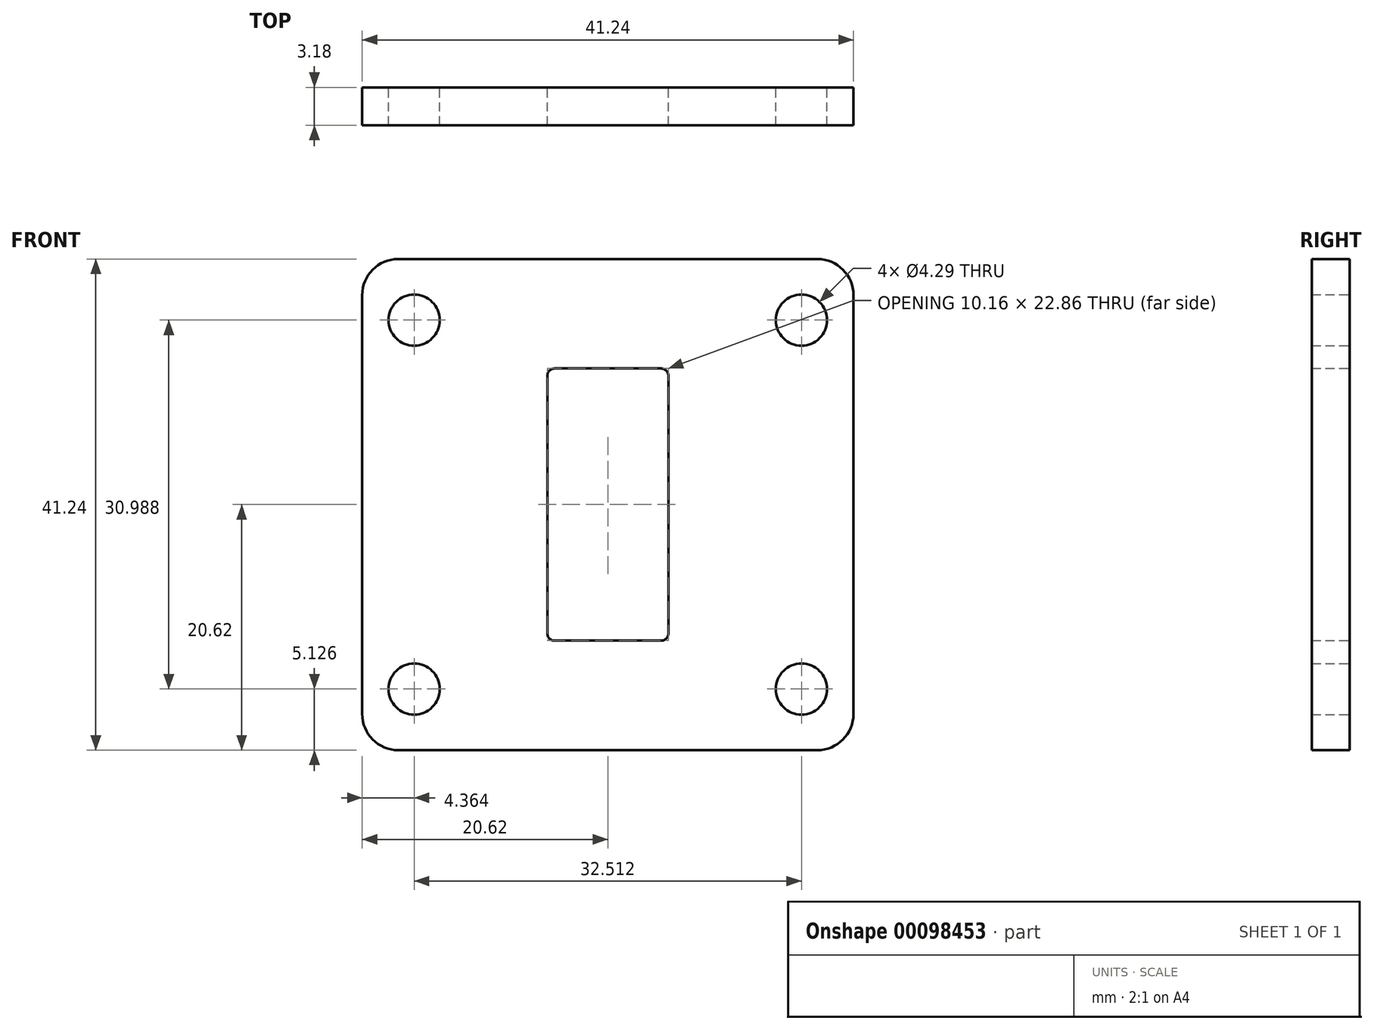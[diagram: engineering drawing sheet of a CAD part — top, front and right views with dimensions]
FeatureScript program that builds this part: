
annotation { "Feature Type Name" : "Feature", "Feature Type Description" : "" }
export const myFeature = defineFeature(function(context is Context, id is Id, definition is map)
    precondition{}
    {
        {
            var Q0;
            Q0=qCreatedBy(makeId("Front.planeOp"),FACE);
            var sketch = newSketch(context, id + "F0", { "sketchPlane" : qUnion([Q0])});
            skLineSegment(sketch, "E0.bottom", {"start": v(-20.62, 20.62) * mm, "end": v(20.62, 20.62) * mm});
            skLineSegment(sketch, "E0.top", {"start": v(-20.62, -20.62) * mm, "end": v(20.62, -20.62) * mm});
            skLineSegment(sketch, "E0.left", {"start": v(-20.62, 20.62) * mm, "end": v(-20.62, -20.62) * mm});
            skLineSegment(sketch, "E0.right", {"start": v(20.62, 20.62) * mm, "end": v(20.62, -20.62) * mm});
            skPoint(sketch, "E0.middle", {"position": v(0, 0) * mm});
            skLineSegment(sketch, "E1.bottom", {"start": v(-5.08, 11.43) * mm, "end": v(5.08, 11.43) * mm});
            skLineSegment(sketch, "E1.top", {"start": v(-5.08, -11.43) * mm, "end": v(5.08, -11.43) * mm});
            skLineSegment(sketch, "E1.left", {"start": v(-5.08, 11.43) * mm, "end": v(-5.08, -11.43) * mm});
            skLineSegment(sketch, "E1.right", {"start": v(5.08, 11.43) * mm, "end": v(5.08, -11.43) * mm});
            skCircle(sketch, "E2", {"center": v(-16.26, 15.5) * mm, "radius": 2.15 * mm});
            skCircle(sketch, "E3", {"center": v(16.26, 15.5) * mm, "radius": 2.15 * mm});
            skCircle(sketch, "E4", {"center": v(-16.26, -15.5) * mm, "radius": 2.15 * mm});
            skCircle(sketch, "E5", {"center": v(16.26, -15.5) * mm, "radius": 2.15 * mm});
            skSolve(sketch);
        }
        {
            var Q0;
            Q0 = qSketchRegion(id + "F0", true);
            extrude(context, id + "F1", {"entities" : qUnion([Q0]), "depth" : 3.17 * mm});
        }
        {
            var Q0;
            Q0=makeQuery(id+"F1.opExtrude","SWEPT_EDGE",EDGE,{"disambiguationData":[OSD([sQuery(id+"F0.wireOp",EDGE,"E0.bottom"),sQuery(id+"F0.wireOp",EDGE,"E0.right")])]});
            var Q1;
            Q1=makeQuery(id+"F1.opExtrude","SWEPT_EDGE",EDGE,{"disambiguationData":[OSD([sQuery(id+"F0.wireOp",EDGE,"E0.bottom"),sQuery(id+"F0.wireOp",EDGE,"E0.left")])]});
            var Q2;
            Q2=makeQuery(id+"F1.opExtrude","SWEPT_EDGE",EDGE,{"disambiguationData":[OSD([sQuery(id+"F0.wireOp",EDGE,"E0.top"),sQuery(id+"F0.wireOp",EDGE,"E0.left")])]});
            var Q3;
            Q3=makeQuery(id+"F1.opExtrude","SWEPT_EDGE",EDGE,{"disambiguationData":[OSD([sQuery(id+"F0.wireOp",EDGE,"E0.top"),sQuery(id+"F0.wireOp",EDGE,"E0.right")])]});
            fillet(context, id + "F2", {"entities" : qUnion([Q0, Q1, Q2, Q3]), "radius" : 3.05 * mm, "tangentPropagation" : true, "allowEdgeOverflow" : false});
        }
        {
            var Q0;
            Q0=makeQuery(id+"F1.opExtrude","SWEPT_EDGE",EDGE,{"disambiguationData":[OSD([sQuery(id+"F0.wireOp",EDGE,"E1.bottom"),sQuery(id+"F0.wireOp",EDGE,"E1.left")])]});
            var Q1;
            Q1=makeQuery(id+"F1.opExtrude","SWEPT_EDGE",EDGE,{"disambiguationData":[OSD([sQuery(id+"F0.wireOp",EDGE,"E1.bottom"),sQuery(id+"F0.wireOp",EDGE,"E1.right")])]});
            var Q2;
            Q2=makeQuery(id+"F1.opExtrude","SWEPT_EDGE",EDGE,{"disambiguationData":[OSD([sQuery(id+"F0.wireOp",EDGE,"E1.top"),sQuery(id+"F0.wireOp",EDGE,"E1.left")])]});
            var Q3;
            Q3=makeQuery(id+"F1.opExtrude","SWEPT_EDGE",EDGE,{"disambiguationData":[OSD([sQuery(id+"F0.wireOp",EDGE,"E1.top"),sQuery(id+"F0.wireOp",EDGE,"E1.right")])]});
            fillet(context, id + "F3", {"entities" : qUnion([Q0, Q1, Q2, Q3]), "radius" : 0.6 * mm, "tangentPropagation" : true, "allowEdgeOverflow" : false});
        }
    });
